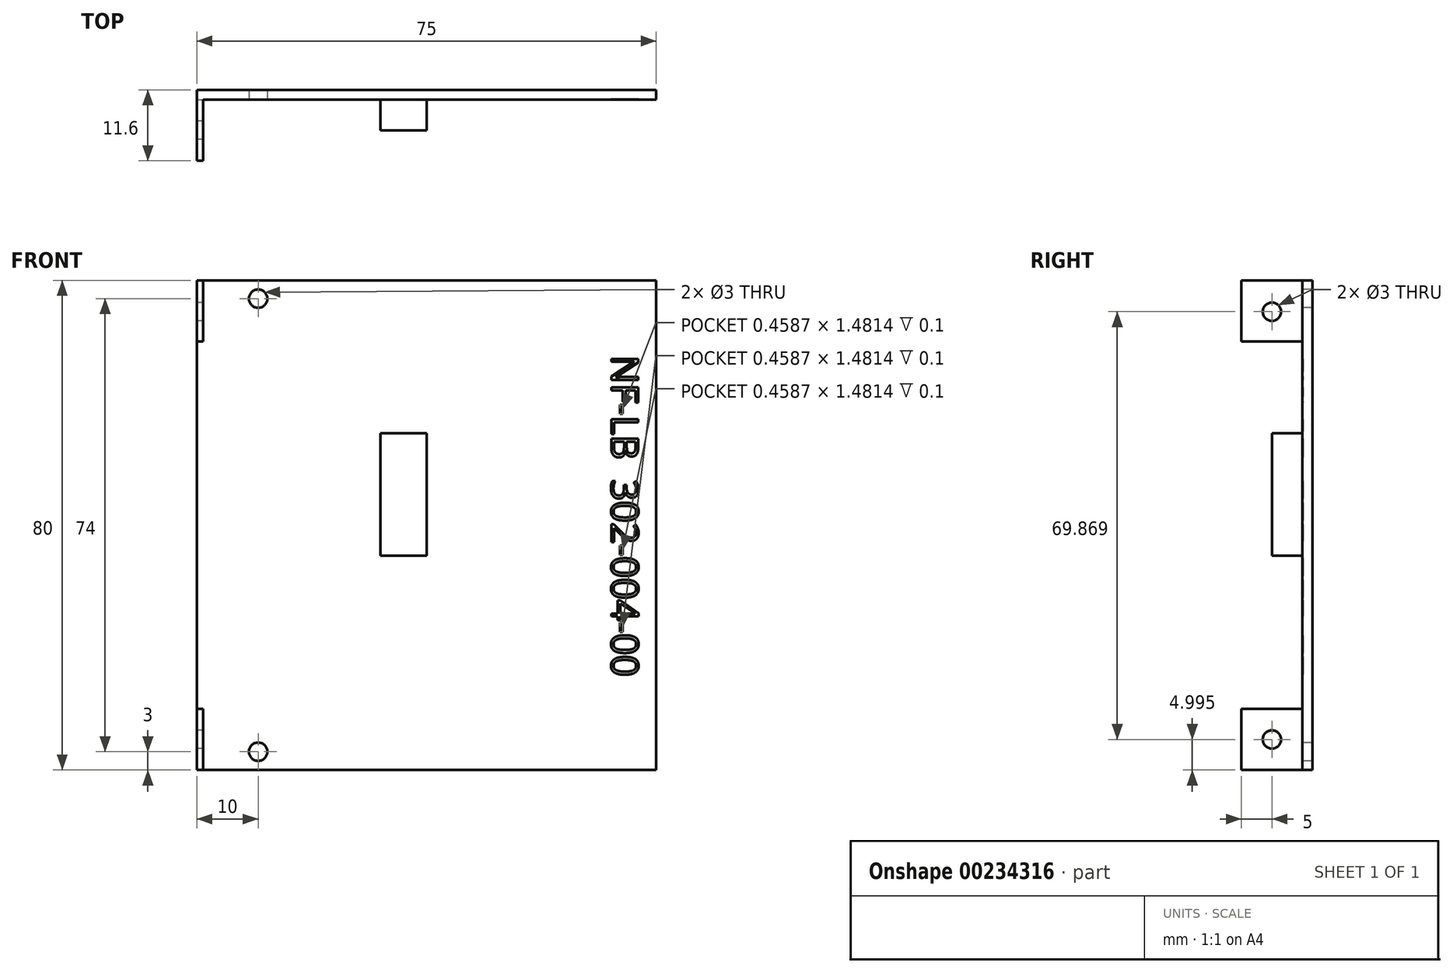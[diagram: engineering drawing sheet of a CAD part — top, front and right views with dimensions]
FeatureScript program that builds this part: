
annotation { "Feature Type Name" : "Feature", "Feature Type Description" : "" }
export const myFeature = defineFeature(function(context is Context, id is Id, definition is map)
    precondition{}
    {
        {
            var Q0;
            Q0=qCreatedBy(makeId("Front.planeOp"),FACE);
            var sketch = newSketch(context, id + "F0", { "sketchPlane" : qUnion([Q0])});
            skLineSegment(sketch, "E0.bottom", {"start": v(37.5, -40) * mm, "end": v(-37.5, -40) * mm});
            skLineSegment(sketch, "E0.top", {"start": v(37.5, 40) * mm, "end": v(-37.5, 40) * mm});
            skLineSegment(sketch, "E0.left", {"start": v(37.5, -40) * mm, "end": v(37.5, 40) * mm});
            skLineSegment(sketch, "E0.right", {"start": v(-37.5, -40) * mm, "end": v(-37.5, 40) * mm});
            skPoint(sketch, "E0.middle", {"position": v(0, 0) * mm});
            skLineSegment(sketch, "E1.bottom", {"start": v(0, -5) * mm, "end": v(-7.5, -5) * mm});
            skLineSegment(sketch, "E1.top", {"start": v(0, 15) * mm, "end": v(-7.5, 15) * mm});
            skLineSegment(sketch, "E1.left", {"start": v(0, -5) * mm, "end": v(0, 15) * mm});
            skLineSegment(sketch, "E1.right", {"start": v(-7.5, -5) * mm, "end": v(-7.5, 15) * mm});
            skPoint(sketch, "E1.middle", {"position": v(-3.75, 5) * mm});
            skCircle(sketch, "E2", {"center": v(-27.5, 37) * mm, "radius": 1.5 * mm});
            skCircle(sketch, "E3.MirrorC", {"center": v(-27.5, -37) * mm, "radius": 1.5 * mm});
            skLineSegment(sketch, "E4", {"start": v(-37.5, 30) * mm, "end": v(-36.5, 30) * mm});
            skLineSegment(sketch, "E5", {"start": v(-36.5, 30) * mm, "end": v(-36.5, 40) * mm});
            skLineSegment(sketch, "E6.MirrorCS", {"start": v(-37.5, -30) * mm, "end": v(-36.5, -30) * mm});
            skLineSegment(sketch, "E7.MirrorCS", {"start": v(-36.5, -30) * mm, "end": v(-36.5, -40) * mm});
            skSolve(sketch);
        }
        {
            var Q0;
            Q0=makeQuery(id+"F0.imprint","IMPRINT",FACE,{"disambiguationData":[TD([[makeQuery(id+"F0.imprint","IMPRINT",EDGE,{"derivedFrom":sQuery(id+"F0.wireOp",EDGE,"E0.bottom")}),-1.0]])]});
            var Q1;
            Q1=makeQuery(id+"F0.imprint","IMPRINT",FACE,{"disambiguationData":[TD([[makeQuery(id+"F0.imprint","IMPRINT",EDGE,{"derivedFrom":sQuery(id+"F0.wireOp",EDGE,"E1.bottom")}),-1.0]])]});
            var Q2;
            {var subQ0=sQuery(id+"F0.wireOp",EDGE,"E0.left");Q2=makeQuery(id+"F0.imprint","IMPRINT",FACE,{"disambiguationData":[TD([[makeQuery(id+"F0.imprint","IMPRINT",EDGE,{"derivedFrom":subQ0}),1.0]])]});}
            var Q3;
            {var subQ4=sQuery(id+"F0.wireOp",EDGE,"E4");Q3=makeQuery(id+"F0.imprint","IMPRINT",FACE,{"disambiguationData":[TD([[makeQuery(id+"F0.imprint","IMPRINT",EDGE,{"derivedFrom":subQ4}),1.0]])]});}
            extrude(context, id + "F1", {"entities" : qUnion([Q0, Q1, Q2, Q3]), "oppositeDirection" : true, "depth" : 1.6 * mm});
        }
        {
            var Q0;
            Q0=makeQuery(id+"F0.imprint","IMPRINT",FACE,{"disambiguationData":[TD([[makeQuery(id+"F0.imprint","IMPRINT",EDGE,{"derivedFrom":sQuery(id+"F0.wireOp",EDGE,"E1.bottom")}),-1.0]])]});
            extrude(context, id + "F2", {"entities" : qUnion([Q0]), "operationType" : NewBodyOperationType.ADD, "depth" : 5 * mm});
        }
        {
            var Q0;
            Q0=makeQuery(id+"F0.imprint","IMPRINT",FACE,{"disambiguationData":[TD([[makeQuery(id+"F0.imprint","IMPRINT",EDGE,{"derivedFrom":sQuery(id+"F0.wireOp",EDGE,"E0.bottom")}),-1.0]])]});
            var sketch = newSketch(context, id + "F3", { "sketchPlane" : qUnion([Q0])});
            skText(sketch, "E8", { "text": "NF-LB  302-004-00", "fontName": "OpenSans-Regular.ttf"});
            const initialGuessF3  = {"E8": [0.03017, 0.02777, 0, -1, 0.00445]};
            skSetInitialGuess(sketch, initialGuessF3);
            skSolve(sketch);
        }
        {
            var Q0;
            Q0 = qSketchRegion(id + "F3", true);
            extrude(context, id + "F4", {"entities" : qUnion([Q0]), "operationType" : NewBodyOperationType.REMOVE, "oppositeDirection" : true, "depth" : .1 * mm});
        }
        {
            var Q0;
            {var subQ4=sQuery(id+"F0.wireOp",EDGE,"E4");Q0=makeQuery(id+"F0.imprint","IMPRINT",FACE,{"disambiguationData":[TD([[makeQuery(id+"F0.imprint","IMPRINT",EDGE,{"derivedFrom":subQ4}),1.0]])]});}
            var Q1;
            {var subQ4=sQuery(id+"F0.wireOp",EDGE,"E6.MirrorCS");Q1=makeQuery(id+"F0.imprint","IMPRINT",FACE,{"disambiguationData":[TD([[makeQuery(id+"F0.imprint","IMPRINT",EDGE,{"derivedFrom":subQ4}),-1.0]])]});}
            extrude(context, id + "F5", {"entities" : qUnion([Q0, Q1]), "operationType" : NewBodyOperationType.ADD, "depth" : 10 * mm});
        }
        {
            var Q0;
            {var subQ0=sQuery(id+"F0.wireOp",EDGE,"E0.right");Q0=makeQuery(id+"F5.boolean.opBoolean","MERGE",FACE,{"derivedFrom":[makeQuery(id+"F1.opExtrude","SWEPT_FACE",FACE,{"disambiguationData":[OSD([subQ0])]}),makeQuery(id+"F5.opExtrude","SWEPT_FACE",FACE,{"disambiguationData":[OSD([subQ0]),TDD([makeQuery(id+"F0.imprint","IMPRINT",EDGE,{"disambiguationData":[TD([[makeQuery(id+"F0.imprint","INTERSECT",VERTEX,{"derivedFrom":[sQuery(id+"F0.wireOp",EDGE,"E0.bottom"),subQ0]}),-1.0]])],"derivedFrom":subQ0})])]}),makeQuery(id+"F5.opExtrude","SWEPT_FACE",FACE,{"disambiguationData":[OSD([subQ0]),TDD([makeQuery(id+"F0.imprint","IMPRINT",EDGE,{"disambiguationData":[TD([[makeQuery(id+"F0.imprint","INTERSECT",VERTEX,{"derivedFrom":[sQuery(id+"F0.wireOp",EDGE,"E0.top"),subQ0]}),1.0]])],"derivedFrom":subQ0})])]})]});}
            var sketch = newSketch(context, id + "F6", { "sketchPlane" : qUnion([Q0])});
            skCircle(sketch, "E9", {"center": v(5, 34.86) * mm, "radius": 1.5 * mm});
            skPoint(sketch, "E9.centerSnap0", {"position": v(4.2, 40) * mm});
            skPoint(sketch, "E9.centerSnap1", {"position": v(10, 35) * mm});
            skCircle(sketch, "E10", {"center": v(5, -35) * mm, "radius": 1.5 * mm});
            skPoint(sketch, "E10.centerSnap0", {"position": v(10, -35) * mm});
            skPoint(sketch, "E10.centerSnap1", {"position": v(5, -30) * mm});
            skSolve(sketch);
        }
        {
            var Q0;
            Q0=makeQuery(id+"F6.imprint","IMPRINT",FACE,{"disambiguationData":[TD([[makeQuery(id+"F6.imprint","IMPRINT",EDGE,{"derivedFrom":sQuery(id+"F6.wireOp",EDGE,"E10")}),1.0]])]});
            var Q1;
            Q1=makeQuery(id+"F6.imprint","IMPRINT",FACE,{"disambiguationData":[TD([[makeQuery(id+"F6.imprint","IMPRINT",EDGE,{"derivedFrom":sQuery(id+"F6.wireOp",EDGE,"E9")}),1.0]])]});
            extrude(context, id + "F7", {"entities" : qUnion([Q0, Q1]), "operationType" : NewBodyOperationType.REMOVE, "endBound" : BoundingType.UP_TO_NEXT, "oppositeDirection" : true, "depth" : 25 * mm});
        }
    });
